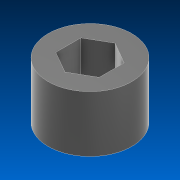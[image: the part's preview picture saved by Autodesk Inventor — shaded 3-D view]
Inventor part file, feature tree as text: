
AUTODESK INVENTOR PART (.ipt)
format: ipt  version: 2022 (Build 260153000, 153)  size: 93,696 bytes
history: native  units: in
note: dims shown in document units (in); Inventor stores cm internally (conversion verified against a paired STEP export)
features: extrude x1, sketch x1
ambient origin geometry x8: Origin, YZ Plane, XZ Plane, XY Plane, X Axis, Y Axis, Z Axis, Center Point
bodies: Solid1 (feature_tree)
feature tree (2):
  extrude  "Extrusion1"  Depth=0.3363in
  sketch  "Sketch1"  dims[d0=0.26in d1=0.5in d2=0.3363in d3=0.0in]
